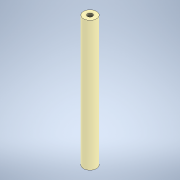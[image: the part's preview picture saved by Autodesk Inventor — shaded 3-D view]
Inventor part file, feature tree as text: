
AUTODESK INVENTOR PART (.ipt)
format: ipt  version: 2021 (Build 250183000, 183)  size: 108,032 bytes
history: native  units: in
note: dims shown in document units (in); Inventor stores cm internally (conversion verified against a paired STEP export)
features: sketch x3, hole x2, extrude x1
ambient origin geometry x8: Origin, YZ Plane, XZ Plane, XY Plane, X Axis, Y Axis, Z Axis, Center Point
bodies: Solid1 (feature_tree)
feature tree (6):
  extrude  "Extrusion1"  TaperAngle=0.0deg  [1 undecoded]
  hole  "Hole1"  [1 undecoded]
  hole  "Hole2"  [1 undecoded]
  sketch  "Sketch1"  dims[d0=0.0in d1=0.0in]
  sketch  "Sketch2"  dims[d2=0.5in d3=5.0in d4=0.0in]
  sketch  "Sketch3"  dims[d5=0.196in d6=0.5in d7=0.375in d8=0.25in d9=0.5635in d10=0.75in d11=0.8108in d12=0.196in d13=0.5in d14=0.375in d15=0.25in d16=0.5635in d17=0.75in d18=0.8108in d19=0.75in d20=0.8108in d21=0.0625in d22=0.75in d23=0.375in]
note: 3 required parameter values undecoded (feature->parameter linkage not recoverable at this tier; creation-order binding heuristic only, values carry confidence <= 0.55)
